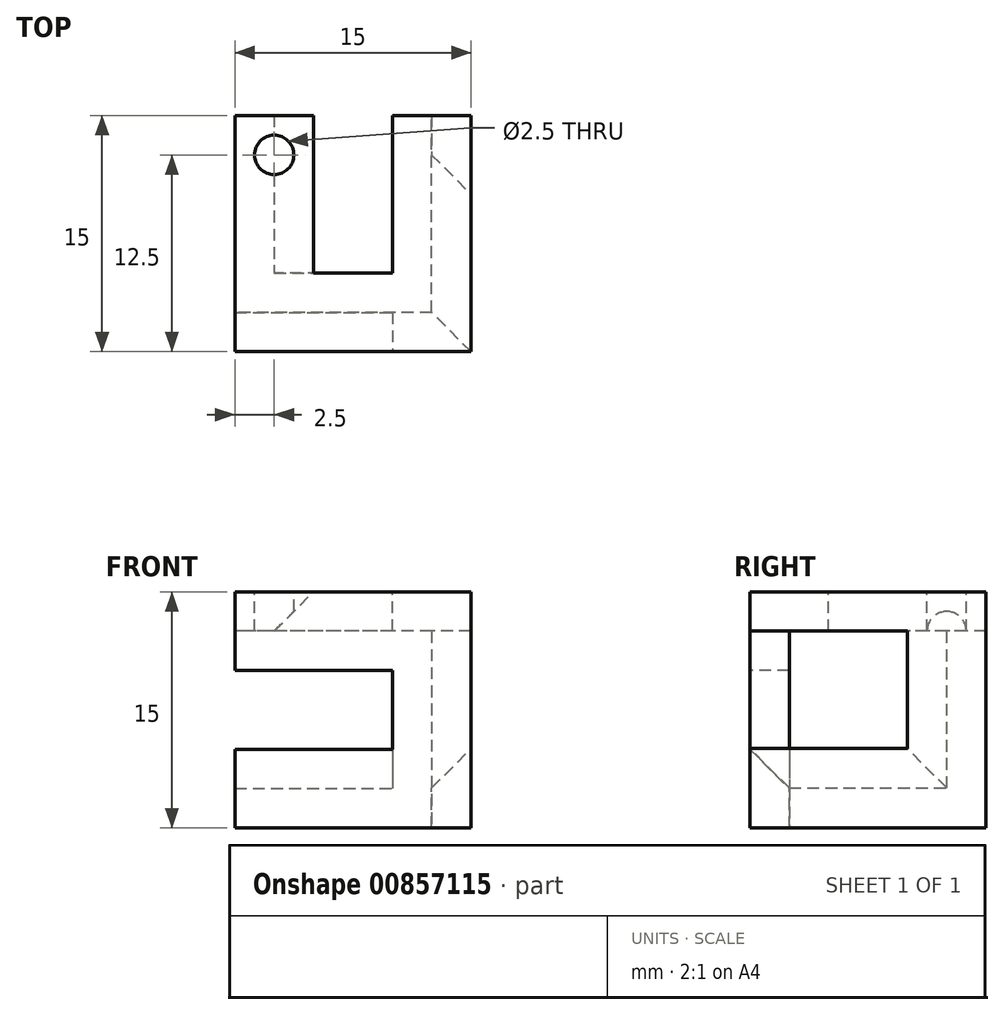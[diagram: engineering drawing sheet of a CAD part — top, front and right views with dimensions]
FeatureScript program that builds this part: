
annotation { "Feature Type Name" : "Feature", "Feature Type Description" : "" }
export const myFeature = defineFeature(function(context is Context, id is Id, definition is map)
    precondition{}
    {
        {
            var Q0;
            Q0=qCreatedBy(makeId("Front.planeOp"),FACE);
            var sketch = newSketch(context, id + "F0", { "sketchPlane" : qUnion([Q0])});
            skPoint(sketch, "E0.middle", {"position": v(0, 0) * mm});
            skLineSegment(sketch, "E1.0", {"start": v(-15, 7.5) * mm, "end": v(-15, 2.5) * mm});
            skLineSegment(sketch, "E2.0", {"start": v(-15, -2.5) * mm, "end": v(-15, -7.5) * mm});
            skLineSegment(sketch, "E3.0", {"start": v(-5, 2.5) * mm, "end": v(-5, -2.5) * mm});
            skLineSegment(sketch, "E4", {"start": v(-15, 7.5) * mm, "end": v(0, 7.5) * mm});
            skLineSegment(sketch, "E5", {"start": v(0, 7.5) * mm, "end": v(0, -7.5) * mm});
            skLineSegment(sketch, "E6", {"start": v(0, -7.5) * mm, "end": v(-15, -7.5) * mm});
            skLineSegment(sketch, "E7", {"start": v(-15, 2.5) * mm, "end": v(-5, 2.5) * mm});
            skLineSegment(sketch, "E8", {"start": v(-15, -2.5) * mm, "end": v(-5, -2.5) * mm});
            skSolve(sketch);
        }
        {
            var Q0;
            Q0=qCreatedBy(makeId("Right.planeOp"),FACE);
            var sketch = newSketch(context, id + "F1", { "sketchPlane" : qUnion([Q0])});
            skLineSegment(sketch, "E9.0", {"start": v(15, -2.46) * mm, "end": v(15, -7.5) * mm});
            skLineSegment(sketch, "E10", {"start": v(0, -7.5) * mm, "end": v(15, -7.5) * mm});
            skLineSegment(sketch, "E11.0", {"start": v(15, 5) * mm, "end": v(15, -2.46) * mm});
            skLineSegment(sketch, "E12.0", {"start": v(15, 7.5) * mm, "end": v(15, 5) * mm});
            skLineSegment(sketch, "E13", {"start": v(0, -2.46) * mm, "end": v(0, -7.5) * mm});
            skLineSegment(sketch, "E14.0", {"start": v(10, 5) * mm, "end": v(10, -2.46) * mm});
            skLineSegment(sketch, "E15", {"start": v(10, -2.46) * mm, "end": v(0, -2.46) * mm});
            skLineSegment(sketch, "E16", {"start": v(10, 5) * mm, "end": v(10, 7.5) * mm});
            skLineSegment(sketch, "E17", {"start": v(10, 7.5) * mm, "end": v(15, 7.5) * mm});
            skSolve(sketch);
        }
        {
            var Q0;
            Q0=makeQuery(id+"F0.imprint","IMPRINT",FACE,{"disambiguationData":[TD([[makeQuery(id+"F0.imprint","IMPRINT",EDGE,{"derivedFrom":sQuery(id+"F0.wireOp",EDGE,"E1.0")}),1.0]])]});
            extrude(context, id + "F2", {"entities" : qUnion([Q0]), "oppositeDirection" : true, "depth" : 2.5 * mm, "offsetDistance" : 25 * mm});
        }
        {
            var Q0;
            Q0=makeQuery(id+"F1.imprint","IMPRINT",FACE,{"disambiguationData":[TD([[makeQuery(id+"F1.imprint","IMPRINT",EDGE,{"derivedFrom":sQuery(id+"F1.wireOp",EDGE,"E9.0")}),-1.0]])]});
            extrude(context, id + "F3", {"entities" : qUnion([Q0]), "operationType" : NewBodyOperationType.ADD, "oppositeDirection" : true, "depth" : 2.5 * mm, "offsetDistance" : 25 * mm});
        }
        {
            var Q0;
            Q0=makeQuery(id+"F2.opExtrude","CAP_EDGE",EDGE,{"disambiguationData":[OSD([sQuery(id+"F0.wireOp",EDGE,"E5")])],"isStart":false});
            var Q1;
            Q1=makeQuery(id+"F5J2HYDWLR33M3B_2.opExtrude","CAP_EDGE",EDGE,{"disambiguationData":[OSD([sQuery(id+"FZmgjiKclZoP5TM_0.wireOp",EDGE,"Clawx5ED-oCS6-UWBB-aM0Q-6W3fPJdrcd4M")])],"isStart":false});
            var Q2;
            Q2=makeQuery(id+"F2.opExtrude","CAP_EDGE",EDGE,{"disambiguationData":[OSD([sQuery(id+"F0.wireOp",EDGE,"E8")])],"isStart":false});
            chamfer(context, id + "F4", {"entities" : qUnion([Q0, Q1, Q2]), "width" : 2.5 * mm});
        }
        {
            var Q0;
            Q0=makeQuery(id+"F3.opExtrude","CAP_EDGE",EDGE,{"disambiguationData":[OSD([sQuery(id+"F1.wireOp",EDGE,"E15")])],"isStart":false});
            var Q1;
            Q1=makeQuery(id+"F3.opExtrude","CAP_EDGE",EDGE,{"disambiguationData":[OSD([sQuery(id+"F1.wireOp",EDGE,"E14.0"),sQuery(id+"F1.wireOp",EDGE,"E16")])],"isStart":false});
            chamfer(context, id + "F5", {"entities" : qUnion([Q0, Q1]), "width" : 2.5 * mm, "tangentPropagation" : true});
        }
        {
            var Q0;
            Q0=makeQuery(id+"F2.opExtrude","SWEPT_FACE",FACE,{"disambiguationData":[OSD([sQuery(id+"F0.wireOp",EDGE,"E4")])]});
            cPlane(context, id + "F6", {"entities" : qUnion([Q0]), "cplaneType" : CPlaneType.OFFSET, "offset" : 0 * mm, "width" : 150 * mm, "height" : 150 * mm});
        }
        {
            var Q0;
            Q0=qCreatedBy(id+"F6.planeOp",FACE);
            var sketch = newSketch(context, id + "F7", { "sketchPlane" : qUnion([Q0])});
            skLineSegment(sketch, "E18.0.0", {"start": v(0, 15) * mm, "end": v(-5, 15) * mm});
            skLineSegment(sketch, "E18.0.1", {"start": v(-5, 15) * mm, "end": v(-5, 5) * mm});
            skLineSegment(sketch, "E18.0.2", {"start": v(-5, 5) * mm, "end": v(-10, 5) * mm});
            skLineSegment(sketch, "E18.0.3", {"start": v(-10, 5) * mm, "end": v(-10, 15) * mm});
            skLineSegment(sketch, "E18.0.4", {"start": v(-10, 15) * mm, "end": v(-15, 15) * mm});
            skLineSegment(sketch, "E18.0.5", {"start": v(-15, 15) * mm, "end": v(-15, 0) * mm});
            skLineSegment(sketch, "E18.0.6", {"start": v(-15, 0) * mm, "end": v(0, 0) * mm});
            skLineSegment(sketch, "E18.0.7", {"start": v(0, 0) * mm, "end": v(0, 15) * mm});
            skPoint(sketch, "E19", {"position": v(-12.5, 12.5) * mm});
            skSolve(sketch);
        }
        {
            var Q0;
            Q0=makeQuery(id+"F7.imprint","IMPRINT",FACE,{"disambiguationData":[TD([[makeQuery(id+"F7.imprint","IMPRINT",EDGE,{"derivedFrom":sQuery(id+"F7.wireOp",EDGE,"E18.0.0")}),1.0]])]});
            extrude(context, id + "F8", {"entities" : qUnion([Q0]), "operationType" : NewBodyOperationType.ADD, "oppositeDirection" : true, "depth" : 2.5 * mm, "offsetDistance" : 25 * mm});
        }
        {
            var Q0;
            Q0=makeQuery(id+"F8.opExtrude","CAP_EDGE",EDGE,{"disambiguationData":[OSD([sQuery(id+"F7.wireOp",EDGE,"E18.0.3")])],"isStart":false});
            chamfer(context, id + "F9", {"entities" : qUnion([Q0]), "width" : 2.5 * mm, "tangentPropagation" : true});
        }
        {
            var Q0;
            Q0=sQuery(id+"F7.wireOp",VERTEX,"E19");
            var Q1;
            Q1=makeQuery(id+"F2.opExtrude","SWEPT_BODY",BODY,{"disambiguationData":[OSD([sQuery(id+"F0.wireOp",EDGE,"E1.0"),sQuery(id+"F0.wireOp",EDGE,"E2.0"),sQuery(id+"F0.wireOp",EDGE,"E3.0"),sQuery(id+"F0.wireOp",EDGE,"E4"),sQuery(id+"F0.wireOp",EDGE,"E5"),sQuery(id+"F0.wireOp",EDGE,"E6"),sQuery(id+"F0.wireOp",EDGE,"E7"),sQuery(id+"F0.wireOp",EDGE,"E8")])]});
            hole(context, id + "F10", {"style" : HoleStyle.SIMPLE, "endStyle" : HoleEndStyle.THROUGH, "holeDiameter" : 2.5 * mm, "majorDiameter" : 5 * mm, "isTappedThrough" : true, "tappedDepth" : 12 * mm, "tapClearance" : 3, "locations" : qUnion([Q0]), "scope" : qUnion([Q1])});
        }
    });
